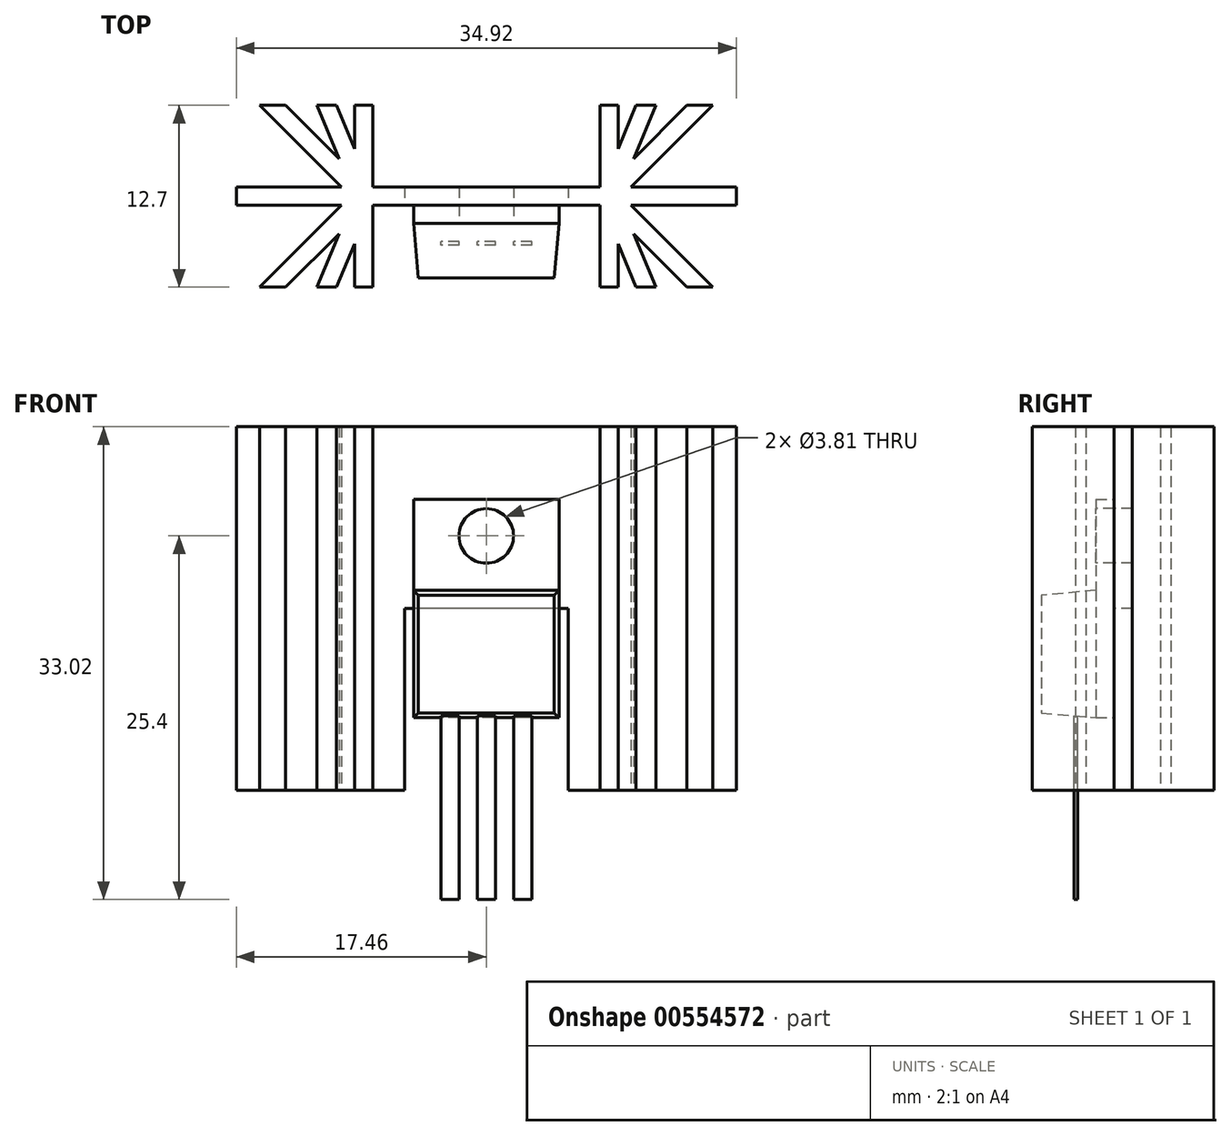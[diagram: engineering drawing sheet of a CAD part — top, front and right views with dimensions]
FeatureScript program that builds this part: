
annotation { "Feature Type Name" : "Feature", "Feature Type Description" : "" }
export const myFeature = defineFeature(function(context is Context, id is Id, definition is map)
    precondition{}
    {
        {
            var Q0;
            Q0=qCreatedBy(makeId("Top.planeOp"),FACE);
            var sketch = newSketch(context, id + "F0", { "sketchPlane" : qUnion([Q0])});
            skLineSegment(sketch, "E0.bottom", {"start": v(17.46, 6.35) * mm, "end": v(-17.46, 6.35) * mm, "construction": true});
            skLineSegment(sketch, "E0.top", {"start": v(17.46, -6.35) * mm, "end": v(-17.46, -6.35) * mm, "construction": true});
            skLineSegment(sketch, "E0.left", {"start": v(17.46, 6.35) * mm, "end": v(17.46, -6.35) * mm, "construction": true});
            skLineSegment(sketch, "E0.right", {"start": v(-17.46, 6.35) * mm, "end": v(-17.46, -6.35) * mm, "construction": true});
            skPoint(sketch, "E0.middle", {"position": v(0, 0) * mm});
            skLineSegment(sketch, "E1", {"start": v(-12.7, 0) * mm, "end": v(12.7, 0) * mm, "construction": true});
            skLineSegment(sketch, "E2.right", {"start": v(-7.94, 0.64) * mm, "end": v(-7.94, -0.64) * mm, "construction": true});
            skLineSegment(sketch, "E3.bottom", {"start": v(7.94, -6.35) * mm, "end": v(9.2, -6.35) * mm});
            skLineSegment(sketch, "E3.top", {"start": v(7.94, 6.35) * mm, "end": v(9.2, 6.35) * mm});
            skLineSegment(sketch, "E4", {"start": v(7.94, 0.64) * mm, "end": v(0, 0.64) * mm});
            skLineSegment(sketch, "E5", {"start": v(0, 0.64) * mm, "end": v(0, -0.64) * mm});
            skLineSegment(sketch, "E6", {"start": v(0, -0.64) * mm, "end": v(7.94, -0.64) * mm});
            skLineSegment(sketch, "E7", {"start": v(0, 0.64) * mm, "end": v(-7.94, 0.64) * mm, "construction": true});
            skLineSegment(sketch, "E8", {"start": v(0, -0.64) * mm, "end": v(-7.94, -0.64) * mm, "construction": true});
            skLineSegment(sketch, "E9", {"start": v(7.94, 0.63) * mm, "end": v(7.94, 6.35) * mm});
            skLineSegment(sketch, "E10", {"start": v(7.94, -0.64) * mm, "end": v(7.94, -6.35) * mm});
            skLineSegment(sketch, "E11", {"start": v(7.94, 0.64) * mm, "end": v(8.57, 0.64) * mm, "construction": true});
            skLineSegment(sketch, "E12", {"start": v(8.57, 0.64) * mm, "end": v(8.57, 0) * mm, "construction": true});
            skLineSegment(sketch, "E13", {"start": v(8.57, 0) * mm, "end": v(14.92, 6.35) * mm, "construction": true});
            skLineSegment(sketch, "E14", {"start": v(8.57, 0) * mm, "end": v(11.2, 6.35) * mm, "construction": true});
            skLineSegment(sketch, "E15", {"start": v(9.2, 3.32) * mm, "end": v(10.46, 6.35) * mm});
            skLineSegment(sketch, "E16", {"start": v(10.46, 6.35) * mm, "end": v(11.84, 6.35) * mm});
            skLineSegment(sketch, "E17", {"start": v(11.84, 6.35) * mm, "end": v(9.2, 0) * mm, "construction": true});
            skLineSegment(sketch, "E18", {"start": v(10.46, 6.35) * mm, "end": v(11.64, 5.86) * mm, "construction": true});
            skLineSegment(sketch, "E19", {"start": v(10.3, 2.62) * mm, "end": v(14.02, 6.35) * mm});
            skLineSegment(sketch, "E20", {"start": v(14.02, 6.35) * mm, "end": v(15.82, 6.35) * mm});
            skLineSegment(sketch, "E21", {"start": v(15.82, 6.35) * mm, "end": v(10.1, 0.63) * mm});
            skLineSegment(sketch, "E22", {"start": v(15.82, 6.35) * mm, "end": v(14.92, 7.25) * mm, "construction": true});
            skLineSegment(sketch, "E23", {"start": v(11.84, 6.35) * mm, "end": v(10.3, 2.62) * mm});
            skLineSegment(sketch, "E24.trimOffspring", {"start": v(9.2, 3.32) * mm, "end": v(9.2, 6.35) * mm});
            skLineSegment(sketch, "E25.MirrorCS", {"start": v(15.82, -6.35) * mm, "end": v(10.1, -0.63) * mm});
            skLineSegment(sketch, "E26.MirrorCS", {"start": v(11.84, -6.35) * mm, "end": v(10.3, -2.62) * mm});
            skLineSegment(sketch, "E27.MirrorCS", {"start": v(10.3, -2.62) * mm, "end": v(14.02, -6.35) * mm});
            skLineSegment(sketch, "E28.MirrorCS", {"start": v(14.02, -6.35) * mm, "end": v(15.82, -6.35) * mm});
            skLineSegment(sketch, "E29.MirrorCS", {"start": v(9.2, -3.32) * mm, "end": v(10.46, -6.35) * mm});
            skLineSegment(sketch, "E30.MirrorCS", {"start": v(9.2, -3.32) * mm, "end": v(9.2, -6.35) * mm});
            skLineSegment(sketch, "E31.MirrorCS", {"start": v(10.46, -6.35) * mm, "end": v(11.84, -6.35) * mm});
            skLineSegment(sketch, "E32.bottom", {"start": v(10.1, -0.63) * mm, "end": v(17.46, -0.63) * mm});
            skLineSegment(sketch, "E32.top", {"start": v(10.1, 0.64) * mm, "end": v(17.46, 0.64) * mm});
            skLineSegment(sketch, "E32.right", {"start": v(17.46, -0.63) * mm, "end": v(17.46, 0.64) * mm});
            skPoint(sketch, "E33.orphan", {"position": v(9.47, 0) * mm});
            skSolve(sketch);
        }
        {
            var Q0;
            Q0 = qSketchRegion(id + "F0", true);
            extrude(context, id + "F1", {"entities" : qUnion([Q0]), "depth" : 25.4 * mm, "offsetDistance" : 25.4 * mm});
        }
        {
            var Q0;
            Q0=makeQuery(id+"F1.opExtrude","SWEPT_BODY",BODY,{"disambiguationData":[OSD([sQuery(id+"F0.wireOp",EDGE,"E3.bottom"),sQuery(id+"F0.wireOp",EDGE,"E3.top"),sQuery(id+"F0.wireOp",EDGE,"E4"),sQuery(id+"F0.wireOp",EDGE,"E5"),sQuery(id+"F0.wireOp",EDGE,"E6"),sQuery(id+"F0.wireOp",EDGE,"E9"),sQuery(id+"F0.wireOp",EDGE,"E10"),sQuery(id+"F0.wireOp",EDGE,"E15"),sQuery(id+"F0.wireOp",EDGE,"E16"),sQuery(id+"F0.wireOp",EDGE,"E19"),sQuery(id+"F0.wireOp",EDGE,"E20"),sQuery(id+"F0.wireOp",EDGE,"E21"),sQuery(id+"F0.wireOp",EDGE,"E23"),sQuery(id+"F0.wireOp",EDGE,"E24.trimOffspring"),sQuery(id+"F0.wireOp",EDGE,"E25.MirrorCS"),sQuery(id+"F0.wireOp",EDGE,"E27.MirrorCS"),sQuery(id+"F0.wireOp",EDGE,"E28.MirrorCS"),sQuery(id+"F0.wireOp",EDGE,"E26.MirrorCS"),sQuery(id+"F0.wireOp",EDGE,"E31.MirrorCS"),sQuery(id+"F0.wireOp",EDGE,"E29.MirrorCS"),sQuery(id+"F0.wireOp",EDGE,"E30.MirrorCS"),sQuery(id+"F0.wireOp",EDGE,"E32.bottom"),sQuery(id+"F0.wireOp",EDGE,"E32.top"),sQuery(id+"F0.wireOp",EDGE,"E32.right")])]});
            var Q1;
            Q1=qCreatedBy(makeId("Right.planeOp"),FACE);
            mirror(context, id + "F2", {"operationType" : NewBodyOperationType.ADD, "entities" : qUnion([Q0]), "mirrorPlane" : qUnion([Q1])});
        }
        {
            var Q0;
            {var subQ0=makeQuery(id+"F1.opExtrude","SWEPT_FACE",FACE,{"disambiguationData":[OSD([sQuery(id+"F0.wireOp",EDGE,"E6")])]});Q0=makeQuery(id+"F2.boolean.opBoolean","MERGE",FACE,{"derivedFrom":[subQ0,makeQuery(id+"F2.opPattern","COPY",FACE,{"derivedFrom":subQ0,"instanceName":"1"})]});}
            var sketch = newSketch(context, id + "F3", { "sketchPlane" : qUnion([Q0])});
            skLineSegment(sketch, "E34.bottom", {"start": v(5.71, 0) * mm, "end": v(-5.71, 0) * mm});
            skLineSegment(sketch, "E34.top", {"start": v(5.72, 12.7) * mm, "end": v(-5.71, 12.7) * mm});
            skLineSegment(sketch, "E34.left", {"start": v(5.72, 0) * mm, "end": v(5.72, 12.7) * mm});
            skLineSegment(sketch, "E34.right", {"start": v(-5.71, 0) * mm, "end": v(-5.71, 12.7) * mm});
            skPoint(sketch, "E34.middle", {"position": v(0, 6.35) * mm});
            skSolve(sketch);
        }
        {
            var Q0;
            Q0=makeQuery(id+"F3.imprint","IMPRINT",FACE,{"disambiguationData":[TD([[makeQuery(id+"F3.imprint","IMPRINT",EDGE,{"derivedFrom":sQuery(id+"F3.wireOp",EDGE,"E34.bottom")}),1.0]])]});
            extrude(context, id + "F4", {"entities" : qUnion([Q0]), "operationType" : NewBodyOperationType.REMOVE, "endBound" : BoundingType.THROUGH_ALL, "oppositeDirection" : true, "depth" : 25.4 * mm, "offsetDistance" : 25.4 * mm});
        }
        {
            var Q0;
            {var subQ0=makeQuery(id+"F1.opExtrude","SWEPT_FACE",FACE,{"disambiguationData":[OSD([sQuery(id+"F0.wireOp",EDGE,"E6")])]});Q0=makeQuery(id+"F2.boolean.opBoolean","MERGE",FACE,{"derivedFrom":[subQ0,makeQuery(id+"F2.opPattern","COPY",FACE,{"derivedFrom":subQ0,"instanceName":"1"})]});}
            var sketch = newSketch(context, id + "F5", { "sketchPlane" : qUnion([Q0])});
            skLineSegment(sketch, "E35.bottom", {"start": v(5.08, 20.32) * mm, "end": v(-5.08, 20.32) * mm});
            skLineSegment(sketch, "E35.top", {"start": v(5.08, 5.08) * mm, "end": v(-5.08, 5.08) * mm});
            skLineSegment(sketch, "E35.left", {"start": v(5.08, 20.32) * mm, "end": v(5.08, 5.08) * mm});
            skLineSegment(sketch, "E35.right", {"start": v(-5.08, 20.32) * mm, "end": v(-5.08, 5.08) * mm});
            skPoint(sketch, "E35.middle", {"position": v(0, 12.7) * mm});
            skSolve(sketch);
        }
        {
            var Q0;
            Q0 = qSketchRegion(id + "F5", true);
            extrude(context, id + "F6", {"entities" : qUnion([Q0]), "depth" : 1.27 * mm, "offsetDistance" : 25.4 * mm});
        }
        {
            var Q0;
            Q0=makeQuery(id+"F6.opExtrude","CAP_FACE",FACE,{"disambiguationData":[OSD([sQuery(id+"F5.wireOp",EDGE,"E35.bottom"),sQuery(id+"F5.wireOp",EDGE,"E35.top"),sQuery(id+"F5.wireOp",EDGE,"E35.left"),sQuery(id+"F5.wireOp",EDGE,"E35.right")])],"isStart":false});
            var sketch = newSketch(context, id + "F7", { "sketchPlane" : qUnion([Q0])});
            skLineSegment(sketch, "E36.bottom", {"start": v(5.08, 13.97) * mm, "end": v(-5.08, 13.97) * mm});
            skLineSegment(sketch, "E36.top", {"start": v(5.08, 5.08) * mm, "end": v(-5.08, 5.08) * mm});
            skLineSegment(sketch, "E36.left", {"start": v(5.08, 13.97) * mm, "end": v(5.08, 5.08) * mm});
            skLineSegment(sketch, "E36.right", {"start": v(-5.08, 13.97) * mm, "end": v(-5.08, 5.08) * mm});
            skPoint(sketch, "E36.middle", {"position": v(0, 9.53) * mm});
            skSolve(sketch);
        }
        {
            var Q0;
            Q0 = qSketchRegion(id + "F7", true);
            extrude(context, id + "F8", {"entities" : qUnion([Q0]), "operationType" : NewBodyOperationType.ADD, "depth" : 3.8 * mm, "offsetDistance" : 25.4 * mm, "hasDraft" : true, "draftAngle" : 5 * degree, "draftPullDirection" : true});
        }
        {
            var Q0;
            Q0=makeQuery(id+"F6.opExtrude","CAP_FACE",FACE,{"disambiguationData":[OSD([sQuery(id+"F5.wireOp",EDGE,"E35.bottom"),sQuery(id+"F5.wireOp",EDGE,"E35.top"),sQuery(id+"F5.wireOp",EDGE,"E35.left"),sQuery(id+"F5.wireOp",EDGE,"E35.right")])],"isStart":false});
            var sketch = newSketch(context, id + "F9", { "sketchPlane" : qUnion([Q0])});
            skSolve(sketch);
        }
        {
            var Q0;
            Q0=makeQuery(id+"F9.imprint","IMPRINT",FACE,{"disambiguationData":[TD([[makeQuery(id+"F9.imprint","IMPRINT",EDGE,{"derivedFrom":makeQuery(id+"F6.opExtrude","CAP_EDGE",EDGE,{"disambiguationData":[OSD([sQuery(id+"F5.wireOp",EDGE,"E35.bottom")])],"isStart":false})}),1.0]])]});
            var sketch = newSketch(context, id + "F10", { "sketchPlane" : qUnion([Q0])});
            skCircle(sketch, "E37", {"center": v(0, 17.78) * mm, "radius": 1.9 * mm});
            skSolve(sketch);
        }
        {
            var Q0;
            Q0 = qSketchRegion(id + "F10", true);
            extrude(context, id + "F11", {"entities" : qUnion([Q0]), "operationType" : NewBodyOperationType.REMOVE, "endBound" : BoundingType.THROUGH_ALL, "oppositeDirection" : true, "depth" : 25.4 * mm, "offsetDistance" : 25.4 * mm});
        }
        {
            var Q0;
            Q0=makeQuery(id+"F6.opExtrude","SWEPT_FACE",FACE,{"disambiguationData":[OSD([sQuery(id+"F5.wireOp",EDGE,"E35.top")])]});
            var sketch = newSketch(context, id + "F12", { "sketchPlane" : qUnion([Q0])});
            skLineSegment(sketch, "E38.bottom", {"start": v(0.63, 3.43) * mm, "end": v(-0.64, 3.43) * mm});
            skLineSegment(sketch, "E38.top", {"start": v(0.64, 3.18) * mm, "end": v(-0.64, 3.18) * mm});
            skLineSegment(sketch, "E38.left", {"start": v(0.64, 3.43) * mm, "end": v(0.64, 3.18) * mm});
            skLineSegment(sketch, "E38.right", {"start": v(-0.64, 3.43) * mm, "end": v(-0.64, 3.18) * mm});
            skPoint(sketch, "E38.middle", {"position": v(0, 3.3) * mm});
            skLineSegment(sketch, "E39.bottom", {"start": v(-1.9, 3.43) * mm, "end": v(-3.18, 3.43) * mm});
            skLineSegment(sketch, "E39.top", {"start": v(-1.9, 3.18) * mm, "end": v(-3.18, 3.18) * mm});
            skLineSegment(sketch, "E39.left", {"start": v(-1.9, 3.43) * mm, "end": v(-1.9, 3.18) * mm});
            skLineSegment(sketch, "E39.right", {"start": v(-3.18, 3.43) * mm, "end": v(-3.18, 3.18) * mm});
            skPoint(sketch, "E39.middle", {"position": v(-2.54, 3.3) * mm});
            skLineSegment(sketch, "E40.bottom", {"start": v(3.18, 3.43) * mm, "end": v(1.9, 3.43) * mm});
            skLineSegment(sketch, "E40.top", {"start": v(3.18, 3.18) * mm, "end": v(1.9, 3.18) * mm});
            skLineSegment(sketch, "E40.left", {"start": v(3.18, 3.43) * mm, "end": v(3.18, 3.18) * mm});
            skLineSegment(sketch, "E40.right", {"start": v(1.9, 3.43) * mm, "end": v(1.9, 3.18) * mm});
            skPoint(sketch, "E40.middle", {"position": v(2.54, 3.3) * mm});
            skLineSegment(sketch, "E41", {"start": v(-2.54, 3.3) * mm, "end": v(0, 3.3) * mm, "construction": true});
            skLineSegment(sketch, "E42", {"start": v(2.54, 3.3) * mm, "end": v(0, 3.3) * mm, "construction": true});
            skSolve(sketch);
        }
        {
            var Q0;
            Q0 = qSketchRegion(id + "F12", true);
            extrude(context, id + "F13", {"entities" : qUnion([Q0]), "operationType" : NewBodyOperationType.ADD, "depth" : 12.7 * mm, "offsetDistance" : 25.4 * mm, "hasSecondDirection" : true, "secondDirectionBound" : BoundingType.UP_TO_NEXT, "secondDirectionOppositeDirection" : true, "secondDirectionDepth" : 25.4 * mm});
        }
    });
